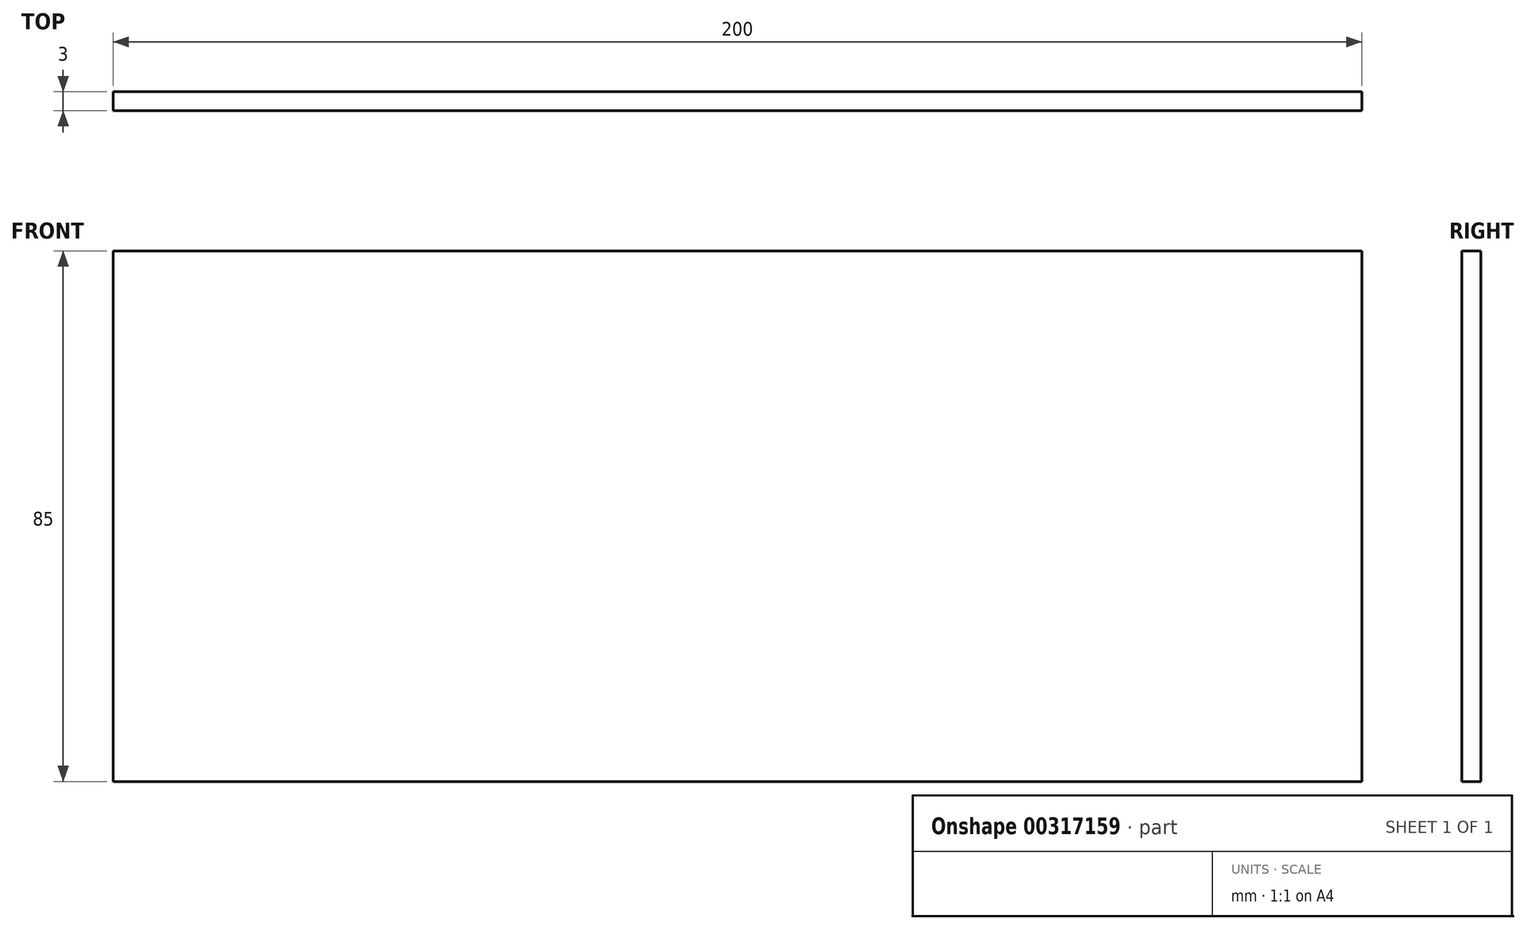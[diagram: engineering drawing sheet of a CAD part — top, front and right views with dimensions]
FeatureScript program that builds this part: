
annotation { "Feature Type Name" : "Feature", "Feature Type Description" : "" }
export const myFeature = defineFeature(function(context is Context, id is Id, definition is map)
    precondition{}
    {
        {
            var Q0;
            Q0=qCreatedBy(makeId("Front.planeOp"),FACE);
            var sketch = newSketch(context, id + "F0", { "sketchPlane" : qUnion([Q0])});
            skLineSegment(sketch, "E0.bottom", {"start": v(100, 42.5) * mm, "end": v(-100, 42.5) * mm});
            skLineSegment(sketch, "E0.top", {"start": v(100, -42.5) * mm, "end": v(-100, -42.5) * mm});
            skLineSegment(sketch, "E0.left", {"start": v(100, 42.5) * mm, "end": v(100, -42.5) * mm});
            skLineSegment(sketch, "E0.right", {"start": v(-100, 42.5) * mm, "end": v(-100, -42.5) * mm});
            skPoint(sketch, "E0.middle", {"position": v(0, 0) * mm});
            skSolve(sketch);
        }
        {
            var Q0;
            Q0 = qSketchRegion(id + "F0", true);
            extrude(context, id + "F1", {"entities" : qUnion([Q0]), "depth" : 3 * mm});
        }
    });
